MODEL slx_9654bdde3b93
KIND model
CONFIG AbsTol = auto
CONFIG EnableMultiTasking = off
CONFIG FixedStep = auto
CONFIG MaxStep = auto
CONFIG MinStep = auto
CONFIG RelTol = 1e-3
CONFIG SampleTimeConstraint = Unconstrained
CONFIG SolverName = VariableStepAuto
CONFIG StartTime = 0.0
CONFIG StopTime = 1000000
BLOCK [BusCreator] Bus Creator
  DisplayOption = bar
  InheritFromInputs = on
  Inputs = 2
BLOCK [Reference] Linear Resistance (SS)  REF=customization_lib/solution/elements/Linear Resistance
(SS)
  SourceBlock = customization_lib/solution/elements/Linear Resistance\n(SS)
  SourceProductName = Customization
  SourceType = Linear Resistance\n(SS)
BLOCK [Reference] Membrane (SS)  REF=customization_lib/membranes/Membrane (SS)
  SourceBlock = customization_lib/membranes/Membrane (SS)
  SourceProductName = Customization
  SourceType = Membrane (SS)
BLOCK [SimscapeProbe] Probe
  BoundBlock = 22
  Variables = {"P.x":{"Probing":"ON"}}
BLOCK [SimscapeProbe] Probe1
  BoundBlock = 18
  Variables = {"mdot_A":{"Probing":"ON"}}
BLOCK [Reference] Reservoir (SS)  REF=customization_lib/solution/elements/Reservoir (SS)
  SourceBlock = customization_lib/solution/elements/Reservoir (SS)
  SourceProductName = Customization
  SourceType = Reservoir (SS)
BLOCK [Reference] Reservoir (SS)1  REF=customization_lib/solution/elements/Reservoir (SS)
  SourceBlock = customization_lib/solution/elements/Reservoir (SS)
  SourceProductName = Customization
  SourceType = Reservoir (SS)
BLOCK [Reference] Solver Configuration  REF=nesl_utility/Solver
Configuration
  SourceBlock = nesl_utility/Solver\nConfiguration
  SourceType = Solver\nConfiguration
BLOCK [ToWorkspace] To Workspace
  FixptAsFi = on
  MaxDataPoints = inf
  SampleTime = -1
  SaveFormat = Timeseries
  VariableName = simout
BLOCK [Reference] Water  REF=customization_lib/solution/elements/Reservoir (SS)
  SourceBlock = customization_lib/solution/elements/Reservoir (SS)
  SourceProductName = Customization
  SourceType = Reservoir (SS)
ANNOTATION (root): <copyright redacted>
LINE Bus Creator:1 -> To Workspace:1
LINE Probe1:1 -> Bus Creator:1
LINE Probe:1 -> Bus Creator:2
PLINE Linear Resistance (SS):LConn1 -- Membrane (SS):RConn1
PLINE Linear Resistance (SS):RConn1 -- Reservoir (SS)1:LConn1
PNET net1: Membrane (SS):LConn1 -- Reservoir (SS):LConn1 -- Solver Configuration:RConn1
PLINE Membrane (SS):RConn2 -- Water:LConn1
note: PNET lines group multi-terminal physical nets as a canonical sorted terminal list (undirected conserving connections); 2-terminal nets keep the pairwise PLINE form
